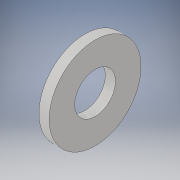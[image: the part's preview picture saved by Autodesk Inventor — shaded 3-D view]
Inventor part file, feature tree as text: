
AUTODESK INVENTOR PART (.ipt)
format: ipt  version: 2018 (Build 220112000, 112)  size: 98,304 bytes
history: native  units: in
note: dims shown in document units (in); Inventor stores cm internally (conversion verified against a paired STEP export)
features: extrude x1, sketch x1
ambient origin geometry x8: Origin, YZ Plane, XZ Plane, XY Plane, X Axis, Y Axis, Z Axis, Center Point
bodies: Solid1 (feature_tree)
feature tree (2):
  extrude  "Extrusion1"  Depth=0.0625in
  sketch  "Sketch1"  dims[d0=0.5625in d1=0.25in d2=0.0625in d3=0.0in]
